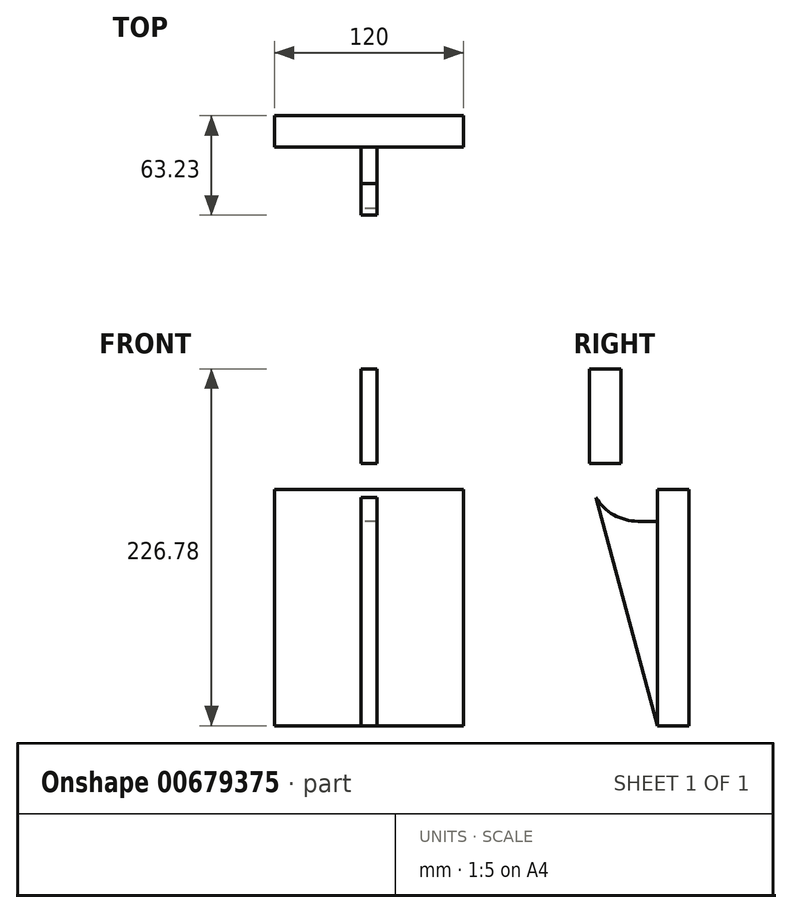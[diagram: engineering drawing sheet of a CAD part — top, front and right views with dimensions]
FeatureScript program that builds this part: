
annotation { "Feature Type Name" : "Feature", "Feature Type Description" : "" }
export const myFeature = defineFeature(function(context is Context, id is Id, definition is map)
    precondition{}
    {
        {
            var Q0;
            Q0=qCreatedBy(makeId("Right.planeOp"),FACE);
            var sketch = newSketch(context, id + "F0", { "sketchPlane" : qUnion([Q0])});
            skLineSegment(sketch, "E0.bottom", {"start": v(-9.23, -74.08) * mm, "end": v(10.77, -74.08) * mm});
            skLineSegment(sketch, "E0.top", {"start": v(-9.23, 75.92) * mm, "end": v(10.77, 75.92) * mm});
            skLineSegment(sketch, "E0.left", {"start": v(-9.23, -74.08) * mm, "end": v(-9.23, 75.92) * mm});
            skLineSegment(sketch, "E0.right", {"start": v(10.77, -74.08) * mm, "end": v(10.77, 75.92) * mm});
            skLineSegment(sketch, "E1.bottom", {"start": v(-52.46, 92.7) * mm, "end": v(-32.46, 92.7) * mm});
            skLineSegment(sketch, "E1.top", {"start": v(-52.46, 152.7) * mm, "end": v(-32.46, 152.7) * mm});
            skLineSegment(sketch, "E1.left", {"start": v(-52.46, 92.7) * mm, "end": v(-52.46, 152.7) * mm});
            skLineSegment(sketch, "E1.right", {"start": v(-32.46, 92.7) * mm, "end": v(-32.46, 152.7) * mm});
            skLineSegment(sketch, "E2", {"start": v(-9.23, 75.92) * mm, "end": v(-21.78, 75.92) * mm});
            skLineSegment(sketch, "E3", {"start": v(-32.46, 92.7) * mm, "end": v(-32.46, 86.83) * mm});
            skPoint(sketch, "E4.centerSnap0", {"position": v(-32.46, 86.83) * mm});
            skPoint(sketch, "E5.orphan", {"position": v(-32.46, 80.96) * mm});
            skPoint(sketch, "E4.center.orphan", {"position": v(-21.78, 86.83) * mm});
            skArc(sketch, "E6", {"start": v(-21.78, 75.92) * mm, "mid": v(-29.4, 79.13) * mm, "end": v(-32.46, 86.83) * mm});
            skLineSegment(sketch, "E7.0", {"start": v(-52.52, 92.7) * mm, "end": v(-52.52, 86.98) * mm});
            skArc(sketch, "E7.1", {"start": v(-21.78, 55.85) * mm, "mid": v(-36.96, 59.87) * mm, "end": v(-48.19, 70.86) * mm});
            skLineSegment(sketch, "E7.2", {"start": v(-9.23, 55.85) * mm, "end": v(-21.78, 55.85) * mm});
            skLineSegment(sketch, "E8", {"start": v(-9.23, -74.08) * mm, "end": v(-52.52, 86.98) * mm});
            skSolve(sketch);
        }
        {
            var Q0;
            {var subQ3=sQuery(id+"F0.wireOp",EDGE,"E0.bottom");Q0=makeQuery(id+"F0.imprint","IMPRINT",FACE,{"disambiguationData":[TD([[makeQuery(id+"F0.imprint","IMPRINT",EDGE,{"derivedFrom":subQ3}),1.0]])]});}
            extrude(context, id + "F1", {"entities" : qUnion([Q0]), "endBound" : BoundingType.SYMMETRIC, "depth" : 120 * mm, "offsetDistance" : 25.4 * mm});
        }
        {
            var Q0;
            Q0=qSketchRegion(id+"F0",true);
            extrude(context, id + "F2", {"entities" : qUnion([Q0]), "operationType" : NewBodyOperationType.ADD, "endBound" : BoundingType.SYMMETRIC, "depth" : 10 * mm, "offsetDistance" : 25.4 * mm});
        }
    });
